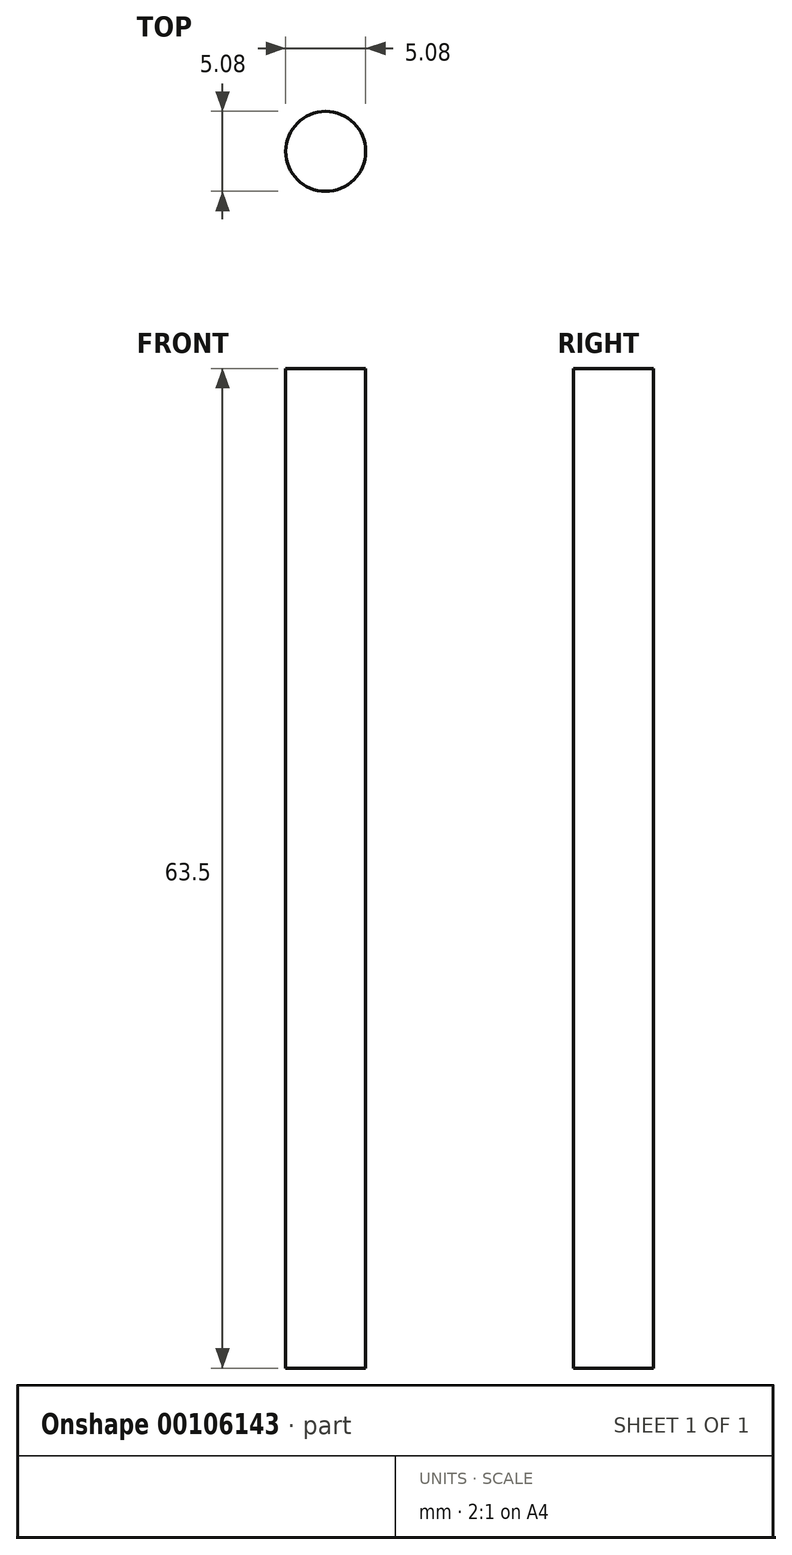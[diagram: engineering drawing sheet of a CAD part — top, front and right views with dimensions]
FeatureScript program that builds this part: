
annotation { "Feature Type Name" : "Feature", "Feature Type Description" : "" }
export const myFeature = defineFeature(function(context is Context, id is Id, definition is map)
    precondition{}
    {
        {
            var Q0;
            Q0=qCreatedBy(makeId("Top.planeOp"),FACE);
            var sketch = newSketch(context, id + "F0", { "sketchPlane" : qUnion([Q0])});
            skCircle(sketch, "E0", {"center": v(0, 0) * mm, "radius": 2.54 * mm});
            skSolve(sketch);
        }
        {
            var Q0;
            Q0=qSketchRegion(id+"F0",true);
            extrude(context, id + "F1", {"entities" : qUnion([Q0]), "depth" : 63.5 * mm});
        }
    });
